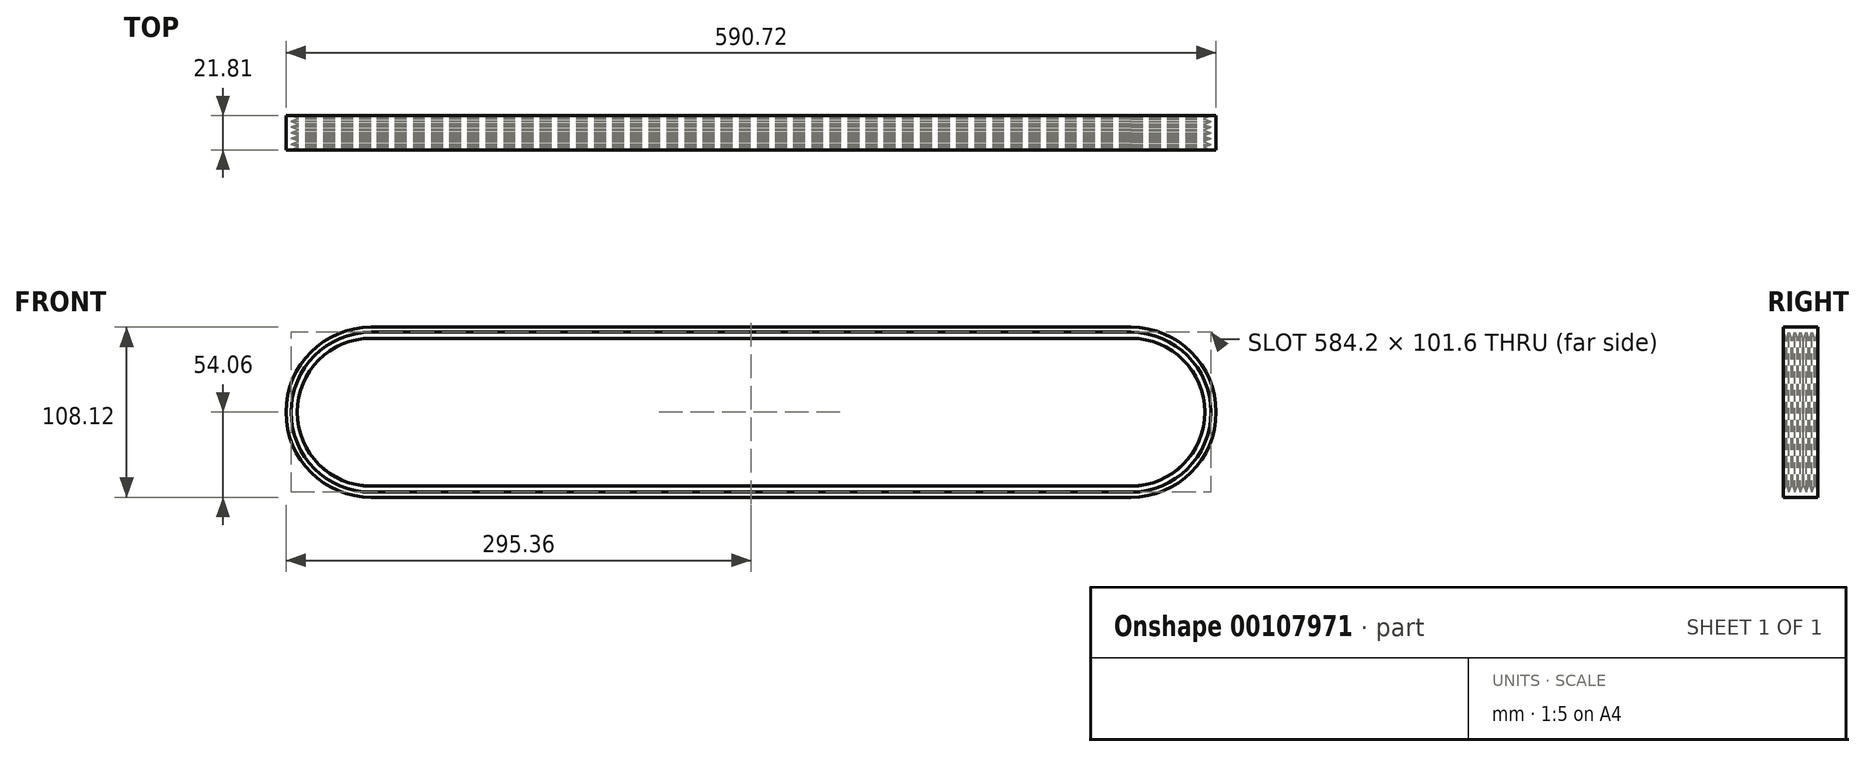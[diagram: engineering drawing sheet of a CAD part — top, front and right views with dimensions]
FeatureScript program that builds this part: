
annotation { "Feature Type Name" : "Feature", "Feature Type Description" : "" }
export const myFeature = defineFeature(function(context is Context, id is Id, definition is map)
    precondition{}
    {
        {
            var Q0;
            Q0=qCreatedBy(makeId("Front.planeOp"),FACE);
            var sketch = newSketch(context, id + "F0", { "sketchPlane" : qUnion([Q0])});
            skArc(sketch, "E0", {"start": v(0, 50.8) * mm, "mid": v(-50.8, 0) * mm, "end": v(0, -50.8) * mm});
            skArc(sketch, "E1", {"start": v(482.6, -50.8) * mm, "mid": v(533.4, 0) * mm, "end": v(482.6, 50.8) * mm});
            skLineSegment(sketch, "E2", {"start": v(482.6, -50.8) * mm, "end": v(0, -50.8) * mm});
            skLineSegment(sketch, "E3", {"start": v(482.6, 50.8) * mm, "end": v(0, 50.8) * mm});
            skSolve(sketch);
        }
        {
            var Q0;
            Q0=qCreatedBy(makeId("Right.planeOp"),FACE);
            var sketch = newSketch(context, id + "F1", { "sketchPlane" : qUnion([Q0])});
            skLineSegment(sketch, "E4.bottom", {"start": v(-21.8, 54.06) * mm, "end": v(0, 54.06) * mm});
            skArc(sketch, "E5", {"start": v(-21.33, 49.49) * mm, "mid": v(-21.34, 49.5) * mm, "end": v(-21.34, 49.5) * mm});
            skLineSegment(sketch, "E6", {"start": v(-21.8, 50.8) * mm, "end": v(-20.4, 46.94) * mm});
            skLineSegment(sketch, "E7", {"start": v(-18.26, 50.8) * mm, "end": v(-16.85, 46.94) * mm});
            skLineSegment(sketch, "E8", {"start": v(-14.08, 49.27) * mm, "end": v(-13.15, 46.93) * mm});
            skLineSegment(sketch, "E9", {"start": v(-14.7, 50.8) * mm, "end": v(-13.15, 46.93) * mm});
            skLineSegment(sketch, "E10", {"start": v(-12.4, 46.93) * mm, "end": v(-11.14, 50.8) * mm});
            skLineSegment(sketch, "E11", {"start": v(-11.14, 50.8) * mm, "end": v(-9.58, 46.93) * mm});
            skLineSegment(sketch, "E12", {"start": v(-8.82, 46.93) * mm, "end": v(-7.35, 50.8) * mm});
            skLineSegment(sketch, "E13", {"start": v(-7.35, 50.8) * mm, "end": v(-6, 46.93) * mm});
            skLineSegment(sketch, "E14", {"start": v(-5.24, 46.93) * mm, "end": v(-3.8, 50.82) * mm});
            skLineSegment(sketch, "E15", {"start": v(-3.8, 50.82) * mm, "end": v(-2.18, 46.92) * mm});
            skLineSegment(sketch, "E16", {"start": v(-1.41, 46.92) * mm, "end": v(0, 50.8) * mm});
            skPoint(sketch, "E17.orphan", {"position": v(0.45, 73.86) * mm});
            skPoint(sketch, "E18.orphan", {"position": v(21.88, 73.86) * mm});
            skLineSegment(sketch, "E19", {"start": v(-21.8, 50.8) * mm, "end": v(-21.8, 54.06) * mm});
            skLineSegment(sketch, "E20", {"start": v(0, 50.8) * mm, "end": v(0, 54.06) * mm});
            skLineSegment(sketch, "E21.trimOffspring", {"start": v(-19.66, 46.94) * mm, "end": v(-18.26, 50.8) * mm});
            skLineSegment(sketch, "E22.trimOffspring", {"start": v(-15.96, 46.94) * mm, "end": v(-14.7, 50.8) * mm});
            skLineSegment(sketch, "E23", {"start": v(-20.4, 46.94) * mm, "end": v(-19.66, 46.94) * mm});
            skLineSegment(sketch, "E24", {"start": v(-16.85, 46.94) * mm, "end": v(-15.96, 46.94) * mm});
            skLineSegment(sketch, "E25", {"start": v(-13.15, 46.93) * mm, "end": v(-12.4, 46.93) * mm});
            skLineSegment(sketch, "E26", {"start": v(-9.58, 46.93) * mm, "end": v(-8.82, 46.93) * mm});
            skLineSegment(sketch, "E27", {"start": v(-6, 46.93) * mm, "end": v(-5.24, 46.93) * mm});
            skLineSegment(sketch, "E28", {"start": v(-2.18, 46.92) * mm, "end": v(-1.41, 46.92) * mm});
            skSolve(sketch);
        }
        {
            var Q0;
            Q0=makeQuery(id+"F1.imprint","IMPRINT",FACE,{"disambiguationData":[TD([[makeQuery(id+"F1.imprint","IMPRINT",EDGE,{"derivedFrom":sQuery(id+"F1.wireOp",EDGE,"E4.bottom")}),-1.0]])]});
            var Q1;
            Q1=sQuery(id+"F0.wireOp",EDGE,"E1");
            var Q2;
            Q2=sQuery(id+"F0.wireOp",EDGE,"E2");
            var Q3;
            Q3=sQuery(id+"F0.wireOp",EDGE,"E0");
            var Q4;
            Q4=sQuery(id+"F0.wireOp",EDGE,"E3");
            sweep(context, id + "F2", {"profiles" : qUnion([Q0]), "path" : qUnion([Q1, Q2, Q3, Q4])});
        }
    });
